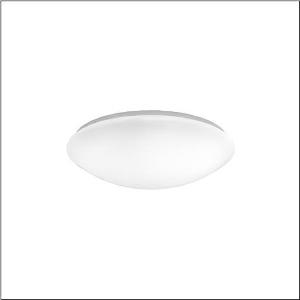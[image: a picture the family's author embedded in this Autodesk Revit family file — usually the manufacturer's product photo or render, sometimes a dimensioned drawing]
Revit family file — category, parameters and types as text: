
# Revit family: round_31_b_5pja130001a
name_source: partatom
category: Lighting Fixtures
units: mm (PartAtom-declared; Revit-internal decimal feet)

## family parameters
Cut with Voids When Loaded = No
Host = Face
Light Source = No
Part Type = Normal
Room Calculation Point = No
Round Connector Dimension = Use Diameter
Shared = No

## types (1)
- Round 31 B (1 x LED, 2700 lm, 21 W, 4000K)
    Apparent Load = 21 VA
    CIE Flux Codes = 42 71 89 88 100
    Color Rendering = 80
    Color Temperature = 4000K
    Default Elevation = 1800 mm
    Description = Round 31 B, wall and ceiling luminaire, primary optical cover: enclosure, of PMMA, light emission: direct distribution, primary light characteristic: symmetric, installation type: surface-mounted, LED, rated luminous flux: 2.700lm, luminous efficacy: 128lm/W, light colour: 840, colour temperature: 4000K, with terminal, 3-pole, max. 2.5mm², mains connection: 230V, AC, 50/60Hz, rated input power: 21W, luminaire housing, round, of steel, white, diameter: 360mm, height: 95mm, protection rating (complete): IP40, insulation class (complete): insulation class I (protective earthing), certification: CE, impact resistance: IK02, packaging unit: 1 piece
    Height = 95 mm
    Lamp = 1 x LED
    Lamp Light Flux = 2700 lm
    Lamp Power = 21 W
    Lamp count = 1
    Length = 360 mm
    Luminous efficacy = 129 lm/W
    Manufacturer = Siteco
    ModVariant = No
    Model = 5PJA130001A
    Mounting Place = Ceiling
    Mounting Type = Surface mounted
    Number of Poles = 1
    OnlyDefault = Yes
    Power Factor = 1
    Product Name = Round 31 B
    Product group = wall and ceiling luminaire
    ProductGroupID = 301
    Protection Class = Protection class I
    Protection Degree = IP 40
    RLX_Detail_Level = 1
    RLX_Emergency_Light_Flux = 0 lm
    RLX_Emergency_Type = 0
    RLX_Emergency_Type_DB = No
    RlxData = <blob elided: 10921 chars, md5=f29273cd>
    Socket = socket
    Standby Power = 0 W
    System Light Flux = 2700 lm
    System Power = 21 W
    Type Comments = Product without accessories
    Type Image = l_1258315.jpg
    URL = http://relux.com
    VarID = ---
    Voltage = 0 V
    Weight = 0.00 kg
    Width = 0 mm  [stored 0 ft]

note: [stored X ft] marks values corroborated as IEEE doubles in the binary element streams (Revit-internal decimal feet)

## geometry (parser evidence)
native form markers: Sweep x10
no freeform markers — native parametric forms only
